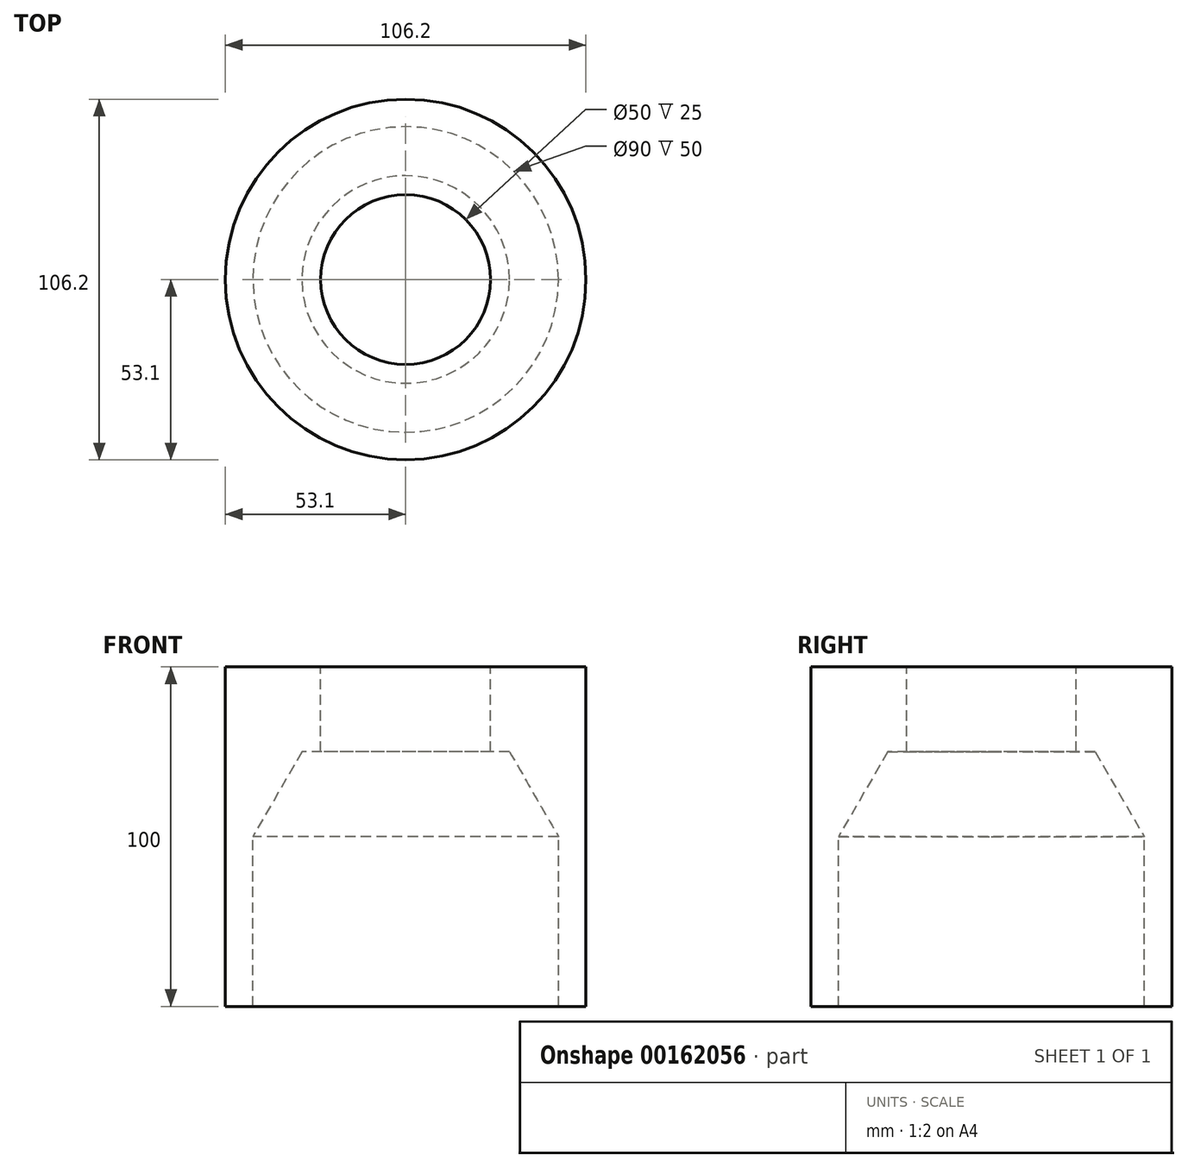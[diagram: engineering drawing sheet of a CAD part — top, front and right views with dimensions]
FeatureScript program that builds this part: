
annotation { "Feature Type Name" : "Feature", "Feature Type Description" : "" }
export const myFeature = defineFeature(function(context is Context, id is Id, definition is map)
    precondition{}
    {
        {
            var Q0;
            Q0=qCreatedBy(makeId("Front.planeOp"),FACE);
            var sketch = newSketch(context, id + "F0", { "sketchPlane" : qUnion([Q0])});
            skLineSegment(sketch, "E0", {"start": v(25, 50) * mm, "end": v(25, 25) * mm});
            skLineSegment(sketch, "E1", {"start": v(25, 25) * mm, "end": v(30.57, 25) * mm});
            skLineSegment(sketch, "E2", {"start": v(30.57, 25) * mm, "end": v(45, 0) * mm});
            skLineSegment(sketch, "E3", {"start": v(45, 0) * mm, "end": v(45, -50) * mm});
            skLineSegment(sketch, "E4", {"start": v(45, -50) * mm, "end": v(53.1, -50) * mm});
            skLineSegment(sketch, "E5", {"start": v(53.1, -50) * mm, "end": v(53.1, 50) * mm});
            skLineSegment(sketch, "E6", {"start": v(53.1, 50) * mm, "end": v(25, 50) * mm});
            skLineSegment(sketch, "E7", {"start": v(0, 55.18) * mm, "end": v(0, -55.18) * mm, "construction": true});
            skSolve(sketch);
        }
        {
            var Q0;
            Q0=makeQuery(id+"F0.imprint","IMPRINT",FACE,{"disambiguationData":[TD([[makeQuery(id+"F0.imprint","IMPRINT",EDGE,{"derivedFrom":sQuery(id+"F0.wireOp",EDGE,"E0")}),1.0]])]});
            var Q1;
            Q1=sQuery(id+"F0.wireOp",EDGE,"E7");
            revolve(context, id + "F1", {"entities" : qUnion([Q0]), "axis" : qUnion([Q1]), "revolveType" : RevolveType.FULL});
        }
    });
